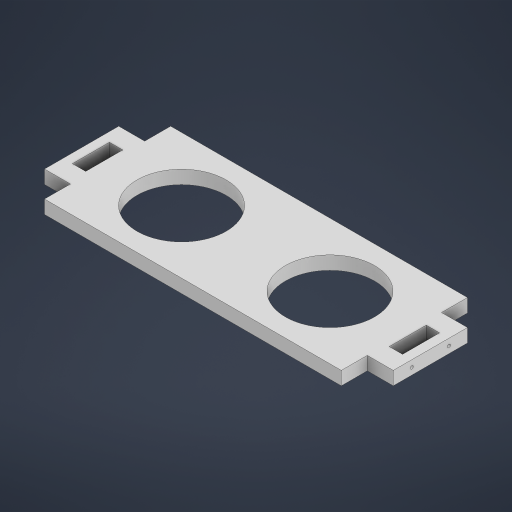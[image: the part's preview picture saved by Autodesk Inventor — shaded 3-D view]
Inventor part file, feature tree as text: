
AUTODESK INVENTOR PART (.ipt)
format: ipt  version: 2024 (Build 280153000, 153)  size: 229,888 bytes
history: native  units: mm
features: extrude x3, sketch x3, other x1
ambient origin geometry x8: Origin, YZ Plane, XZ Plane, XY Plane, X Axis, Y Axis, Z Axis, Center Point
bodies: Body1 (feature_tree)
feature tree (7):
  other  "Sólido1"
  extrude  "Extrusión1"  Depth=18.0mm
  extrude  "Extrusión2"  Depth=35.0mm
  extrude  "Extrusión3"  Depth=50.0mm
  sketch  "Boceto1"  dims[d4=120.0mm d5=18.0mm]
  sketch  "Boceto2"  dims[d6=35.0mm d7=35.0mm]
  sketch  "Boceto3"  dims[d8=35.0mm d9=50.0mm d10=25.0mm d11=12.5mm d12=100.0mm d13=18.0mm d14=0.0mm d15=470.0mm d16=12.5mm d17=18.0mm d18=4.0mm d19=4.0mm d20=9.0mm d21=9.0mm d22=25.0mm d23=50.0mm d24=10.0mm d25=0.0mm d26=4.0mm d27=4.0mm d28=10.0mm d29=0.0mm]
